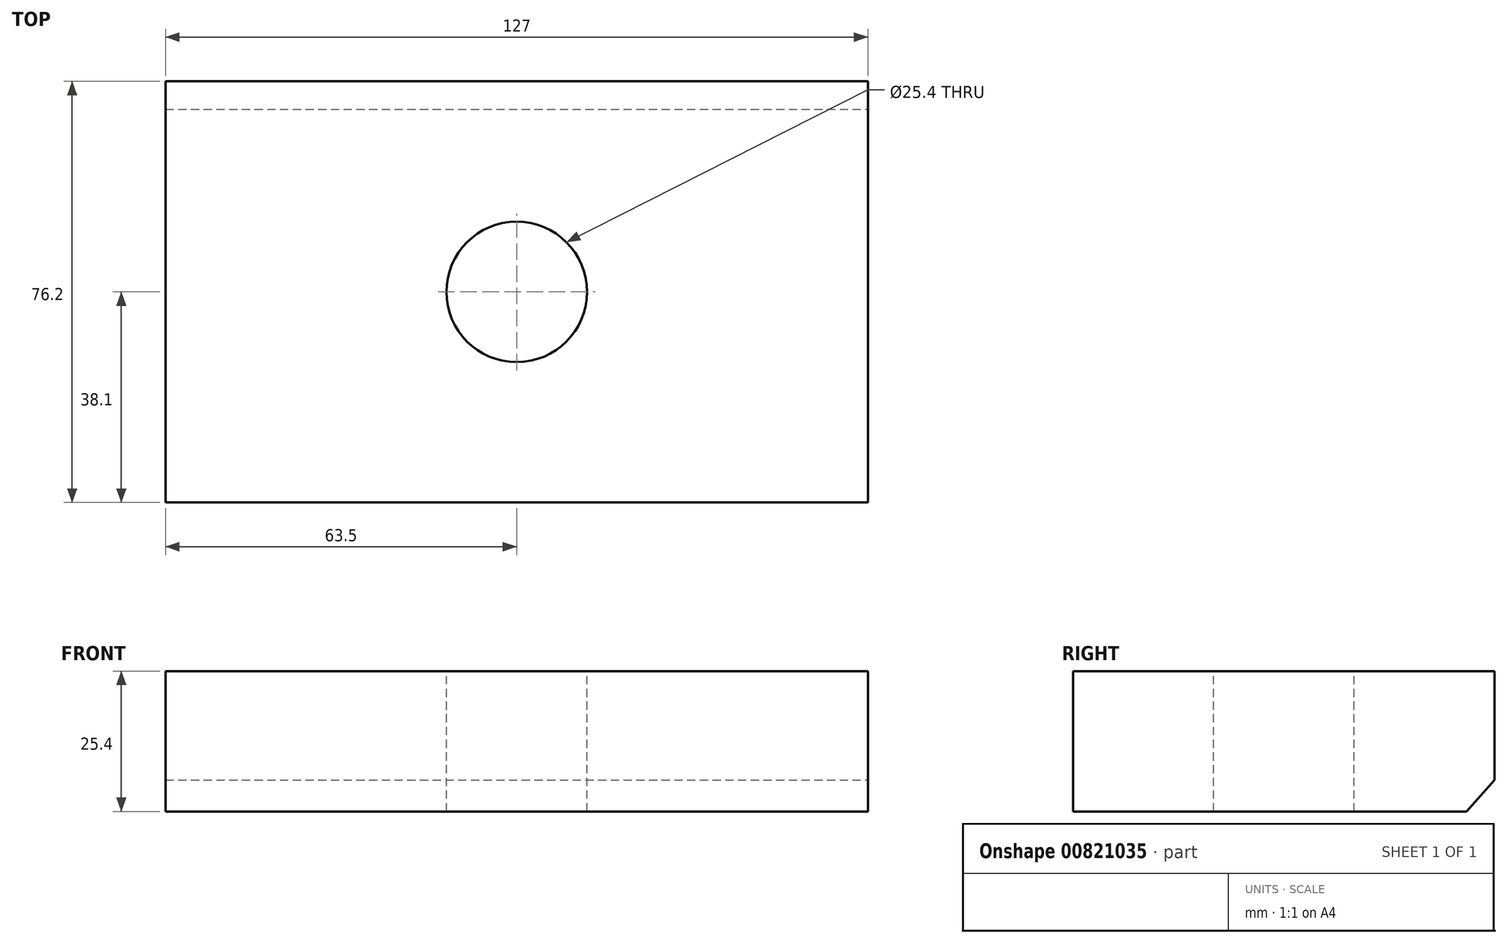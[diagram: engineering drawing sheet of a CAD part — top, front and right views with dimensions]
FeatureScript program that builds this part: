
annotation { "Feature Type Name" : "Feature", "Feature Type Description" : "" }
export const myFeature = defineFeature(function(context is Context, id is Id, definition is map)
    precondition{}
    {
        {
            var Q0;
            Q0=qCreatedBy(makeId("Top.planeOp"),FACE);
            var sketch = newSketch(context, id + "F0", { "sketchPlane" : qUnion([Q0])});
            skLineSegment(sketch, "E0.bottom", {"start": v(63.5, 38.1) * mm, "end": v(-63.5, 38.1) * mm});
            skLineSegment(sketch, "E0.top", {"start": v(63.5, -38.1) * mm, "end": v(-63.5, -38.1) * mm});
            skLineSegment(sketch, "E0.left", {"start": v(63.5, 38.1) * mm, "end": v(63.5, -38.1) * mm});
            skLineSegment(sketch, "E0.right", {"start": v(-63.5, 38.1) * mm, "end": v(-63.5, -38.1) * mm});
            skPoint(sketch, "E0.middle", {"position": v(0, 0) * mm});
            skCircle(sketch, "E1", {"center": v(0, 0) * mm, "radius": 19.05 * mm});
            skSolve(sketch);
        }
        {
            var Q0;
            Q0=makeQuery(id+"F0.imprint","IMPRINT",FACE,{"disambiguationData":[TD([[makeQuery(id+"F0.imprint","IMPRINT",EDGE,{"derivedFrom":sQuery(id+"F0.wireOp",EDGE,"E0.bottom")}),1.0]])]});
            var Q1;
            Q1=makeQuery(id+"F0.imprint","IMPRINT",FACE,{"disambiguationData":[TD([[makeQuery(id+"F0.imprint","IMPRINT",EDGE,{"derivedFrom":sQuery(id+"F0.wireOp",EDGE,"E1")}),1.0]])]});
            extrude(context, id + "F1", {"entities" : qUnion([Q0, Q1]), "depth" : 25.4 * mm, "offsetDistance" : 25.4 * mm});
        }
        {
            var Q0;
            Q0=makeQuery(id+"F1.opExtrude","CAP_FACE",FACE,{"disambiguationData":[OSD([sQuery(id+"F0.wireOp",EDGE,"E0.bottom"),sQuery(id+"F0.wireOp",EDGE,"E0.top"),sQuery(id+"F0.wireOp",EDGE,"E0.left"),sQuery(id+"F0.wireOp",EDGE,"E0.right")])],"isStart":false});
            var sketch = newSketch(context, id + "F2", { "sketchPlane" : qUnion([Q0])});
            skCircle(sketch, "E2", {"center": v(0, 0) * mm, "radius": 12.7 * mm});
            skSolve(sketch);
        }
        {
            var Q0;
            Q0=makeQuery(id+"F2.imprint","IMPRINT",FACE,{"disambiguationData":[TD([[makeQuery(id+"F2.imprint","IMPRINT",EDGE,{"derivedFrom":sQuery(id+"F2.wireOp",EDGE,"E2")}),1.0]])]});
            extrude(context, id + "F3", {"entities" : qUnion([Q0]), "operationType" : NewBodyOperationType.REMOVE, "oppositeDirection" : true, "depth" : 25.4 * mm, "offsetDistance" : 25.4 * mm});
        }
        {
            var Q0;
            Q0=makeQuery(id+"F1.opExtrude","SWEPT_FACE",FACE,{"disambiguationData":[OSD([sQuery(id+"F0.wireOp",EDGE,"E0.left")])]});
            var sketch = newSketch(context, id + "F4", { "sketchPlane" : qUnion([Q0])});
            skLineSegment(sketch, "E3", {"start": v(38.1, 5.68) * mm, "end": v(33.02, 0) * mm});
            skLineSegment(sketch, "E4", {"start": v(38.1, 5.68) * mm, "end": v(38.1, 0) * mm});
            skLineSegment(sketch, "E5", {"start": v(38.1, 0) * mm, "end": v(33.02, 0) * mm});
            skSolve(sketch);
        }
        {
            var Q0;
            Q0=makeQuery(id+"F4.imprint","IMPRINT",FACE,{"disambiguationData":[TD([[makeQuery(id+"F4.imprint","IMPRINT",EDGE,{"derivedFrom":sQuery(id+"F4.wireOp",EDGE,"E3")}),1.0]])]});
            extrude(context, id + "F5", {"entities" : qUnion([Q0]), "operationType" : NewBodyOperationType.REMOVE, "oppositeDirection" : true, "depth" : 128.78 * mm, "offsetDistance" : 25.4 * mm});
        }
    });
